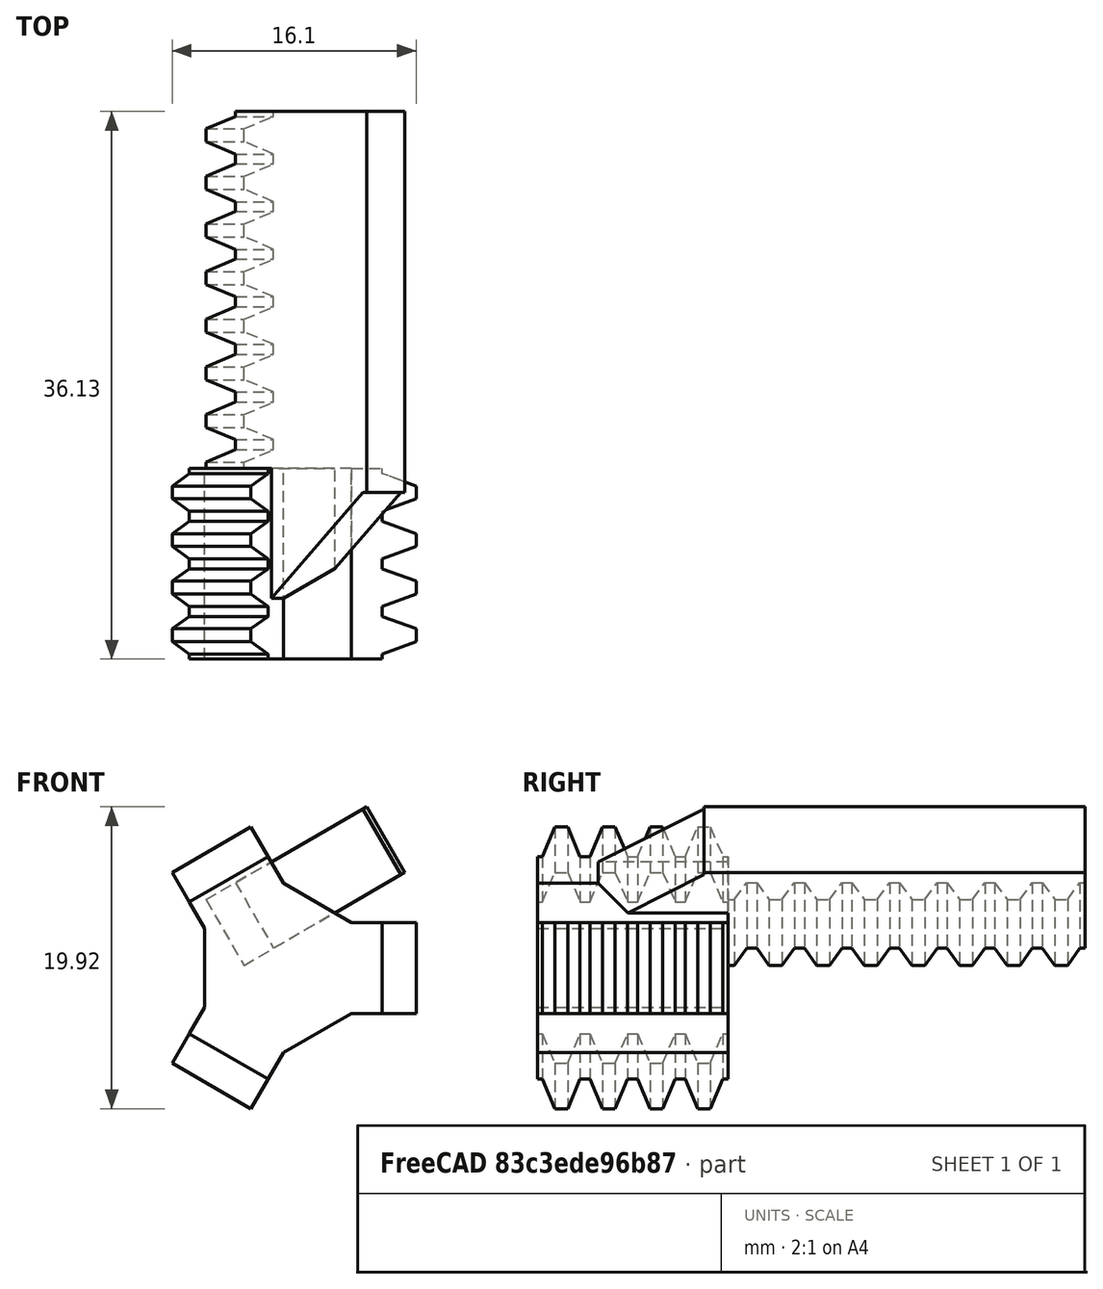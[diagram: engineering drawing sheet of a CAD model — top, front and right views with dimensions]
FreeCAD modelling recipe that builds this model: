
FCSTD DOCUMENT  (FreeCAD 1.0R39319 (Git))
Label: GripperMainShaft
License: All rights reserved
LicenseURL: https://en.wikipedia.org/wiki/All_rights_reserved
objects: PartDesign::FeaturePython×2, PartDesign::Chamfer×2, PartDesign::PolarPattern×1, PartDesign::Body×1
note: 13 computed .brp shape members not serialized (recipe doc carries the construction recipe); baked Part::Feature solids carry a one-line shape summary decoded from their .brp

FEATURE [PartDesign::FeaturePython] InvoluteRack  # WARN: FeaturePython — macro-defined, semantics opaque (R4)
  AttacherType = Attacher::AttachEngine3D
  Placement = pos=(8,0,-3) rot=(0,0,1;0rad)
  Suppressed = false
  add_endings = true
  clearance = 0.25
  double_helix = false
  head = 0
  head_fillet = 0
  height = 6
  helix_angle = 0
  module = 1
  num_teeth = 4
  pressure_angle = 20
  properties_from_tool = false
  root_fillet = 0
  simplified = false
  thickness = 8
  transverse_pitch = 3.14159
  version = 1.3.0
FEATURE [PartDesign::PolarPattern] PolarPattern
  Angle = 360
  Axis = -> Y_Axis
  BaseFeature = -> InvoluteRack
  Mode = 0
  Occurrences = 3
  Offset = 120
  Placement = pos=(8,0,-3) rot=(0,0,1;0rad)
  Refine = true
  Suppressed = false
  TransformMode = 1
FEATURE [PartDesign::Chamfer] Chamfer
  Angle = 45
  Base = -> PolarPattern [Edge41,Edge133,Edge19]
  BaseFeature = -> PolarPattern
  ChamferType = 0
  FlipDirection = false
  Placement = pos=(8,0,-3) rot=(0,0,1;0rad)
  Refine = true
  Size = 3
  Size2 = 1
  SupportTransform = false
  Suppressed = false
  UseAllEdges = false
FEATURE [PartDesign::FeaturePython] InvoluteRack001  # WARN: FeaturePython — macro-defined, semantics opaque (R4)
  AttacherType = Attacher::AttachEngine3D
  BaseFeature = -> Chamfer
  Placement = pos=(-4,11,5) rot=(0,1,0;2.61799rad)
  Suppressed = false
  add_endings = true
  clearance = 0.25
  double_helix = false
  head = 0
  head_fillet = 0
  height = 5
  helix_angle = 0
  module = 1
  num_teeth = 8
  pressure_angle = 20
  properties_from_tool = false
  root_fillet = 0
  simplified = false
  thickness = 10
  transverse_pitch = 3.14159
  version = 1.3.0
FEATURE [PartDesign::Chamfer] Chamfer001
  Angle = 45
  Base = -> InvoluteRack001 [Edge154]
  BaseFeature = -> InvoluteRack001
  ChamferType = 0
  FlipDirection = false
  Placement = pos=(-4,11,5) rot=(0,1,0;2.61799rad)
  Refine = true
  Size = 7
  Size2 = 1
  SupportTransform = false
  Suppressed = false
  UseAllEdges = false
FEATURE [PartDesign::Body] Body  label="GripperMainShaft"
  AllowCompound = false
  Group = -> [InvoluteRack,PolarPattern,Chamfer,InvoluteRack001,Chamfer001]
  Origin = -> Origin
  Tip = -> Chamfer001
